# Revit family: Bath-Freestanding-KOHLER-Vintage-K-700
name_source: partatom
category: Plumbing Fixtures
revit_build: Autodesk Revit 2015 (Build: 20140606_1530(x64)
units: mm (PartAtom-declared; Revit-internal decimal feet)

## types (5) — shared parameters
ADA Compliant = No
Assembly Code = D2010500
CW Connection = No
Cold Water Inlet = Cold Water Inlet
Date Modified = 02/19/2018
Default Elevation = 0"
Description = 72inch x 42inch freestanding bath
HW Connection = No
Height = 21 3/16"
Hot Water Inlet = Hot Water Inlet
Length = 72"
Manufacturer = KOHLER Co.
MasterFormat 1995 = 15410
MasterFormat 2004 = 22.41.19
Material = Enameled Cast Iron
Product Documentation Link = http://www.us.kohler.com
Product Name = Vintage
Product Page URL = http://www.us.kohler.com
URL = https://www.us.kohler.com
Vent Connection = No
Waste Water Outlet = Waste Water Outlet
Width = 42"

## per-type parameters (varying)
| type | Finish | Model | Type | Waste Connection |
| 0-White | Kohler-Enameled_Cast_Iron-0-White | K-700-0 | 1 | No |
| 96-Biscuit | Kohler-Enameled_Cast_Iron-96-Biscuit | K-700-96 | 2 | Yes |
| 47-Almond | Kohler-Enameled_Cast_Iron-47-Almond | K-700-47 | 3 | Yes |
| NY-Dune | Kohler-Enameled_Cast_Iron-NY-Dune | K-700-NY | 4 | Yes |
| G9-Sandbar | Kohler-Enameled_Cast_Iron-G9-Sandbar | K-700-G9 | 5 | Yes |

## geometry (parser evidence)
native form markers: Sweep x6
no freeform markers — native parametric forms only
